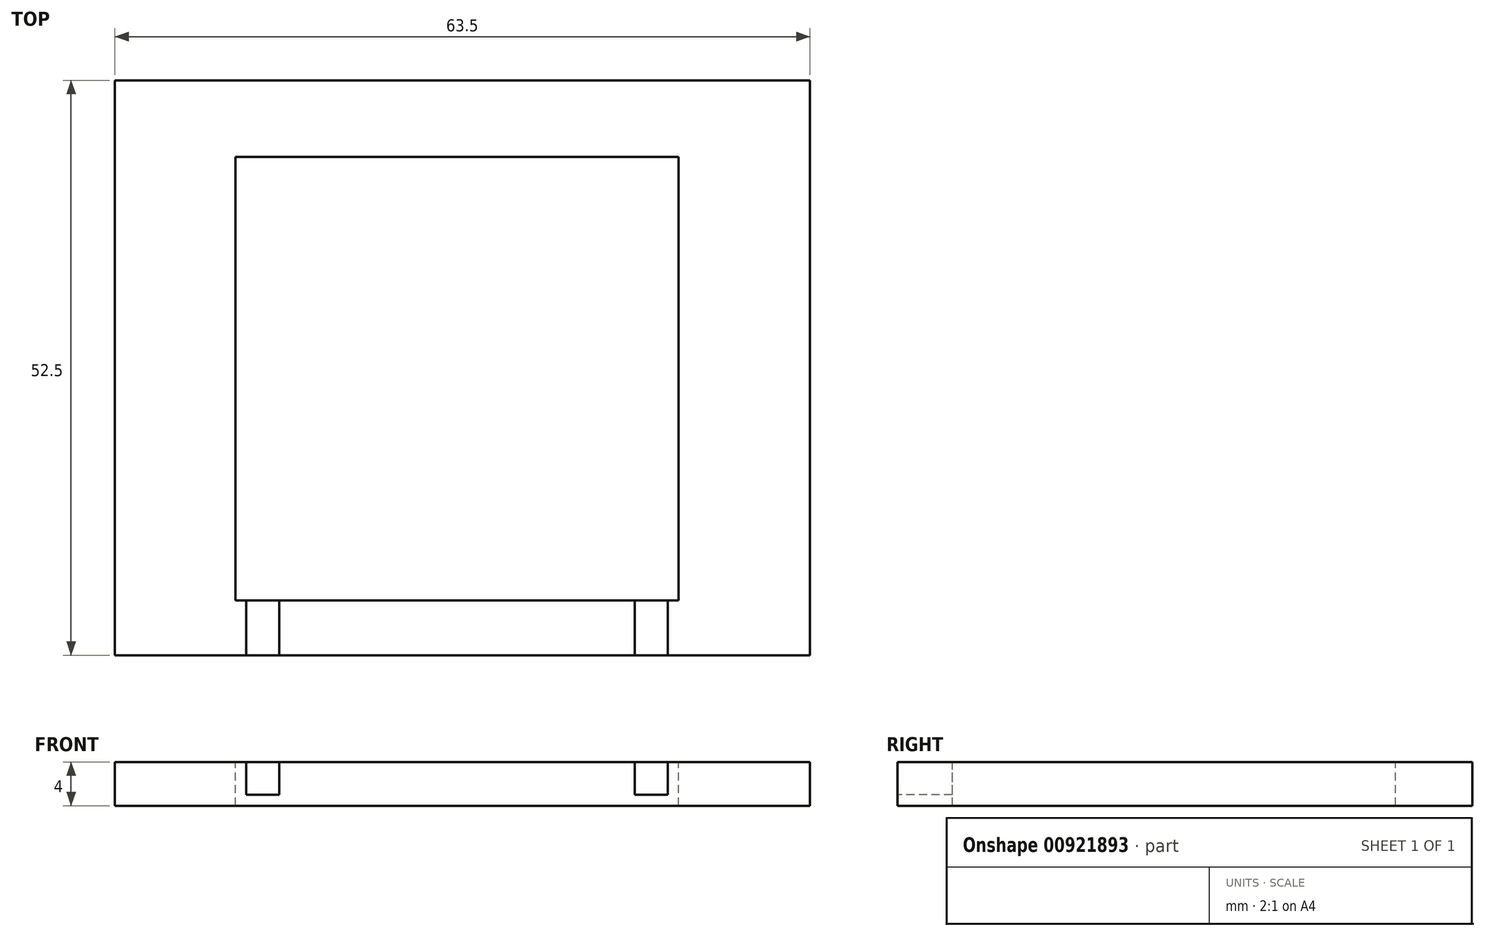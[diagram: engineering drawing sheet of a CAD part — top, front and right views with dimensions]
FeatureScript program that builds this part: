
annotation { "Feature Type Name" : "Feature", "Feature Type Description" : "" }
export const myFeature = defineFeature(function(context is Context, id is Id, definition is map)
    precondition{}
    {
        {
            var Q0;
            Q0=qCreatedBy(makeId("Top.planeOp"),FACE);
            var sketch = newSketch(context, id + "F0", { "sketchPlane" : qUnion([Q0])});
            skLineSegment(sketch, "E0.bottom", {"start": v(0, 0) * mm, "end": v(63.5, 0) * mm});
            skLineSegment(sketch, "E0.top", {"start": v(0, 52.5) * mm, "end": v(63.5, 52.5) * mm});
            skLineSegment(sketch, "E0.left", {"start": v(0, 0) * mm, "end": v(0, 52.5) * mm});
            skLineSegment(sketch, "E0.right", {"start": v(63.5, 0) * mm, "end": v(63.5, 52.5) * mm});
            skSolve(sketch);
        }
        {
            var Q0;
            Q0 = qSketchRegion(id + "F0", true);
            var Q1;
            Q1=makeQuery(id+"F0.imprint","IMPRINT",FACE,{"disambiguationData":[TD([[makeQuery(id+"F0.imprint","IMPRINT",EDGE,{"derivedFrom":sQuery(id+"F0.wireOp",EDGE,"E0.bottom")}),1.0]])]});
            extrude(context, id + "F1", {"entities" : qUnion([Q0, Q1]), "depth" : 4 * mm, "offsetDistance" : 25 * mm});
        }
        {
            var Q0;
            Q0=makeQuery(id+"F1.opExtrude","CAP_FACE",FACE,{"disambiguationData":[OSD([sQuery(id+"F0.wireOp",EDGE,"E0.bottom"),sQuery(id+"F0.wireOp",EDGE,"E0.top"),sQuery(id+"F0.wireOp",EDGE,"E0.left"),sQuery(id+"F0.wireOp",EDGE,"E0.right")])],"isStart":false});
            var sketch = newSketch(context, id + "F2", { "sketchPlane" : qUnion([Q0])});
            skLineSegment(sketch, "E1.bottom", {"start": v(11, 5) * mm, "end": v(51.5, 5) * mm});
            skLineSegment(sketch, "E1.top", {"start": v(11, 45.5) * mm, "end": v(51.5, 45.5) * mm});
            skLineSegment(sketch, "E1.left", {"start": v(11, 5) * mm, "end": v(11, 45.5) * mm});
            skLineSegment(sketch, "E1.right", {"start": v(51.5, 5) * mm, "end": v(51.5, 45.5) * mm});
            skLineSegment(sketch, "E2", {"start": v(12, 5) * mm, "end": v(12, 0) * mm});
            skLineSegment(sketch, "E3", {"start": v(15, 5) * mm, "end": v(15, 0) * mm});
            skLineSegment(sketch, "E4", {"start": v(47.5, 5) * mm, "end": v(47.5, 0) * mm});
            skLineSegment(sketch, "E5", {"start": v(50.5, 5) * mm, "end": v(50.5, 0) * mm});
            skSolve(sketch);
        }
        {
            var Q0;
            {var subQ0=sQuery(id+"F2.wireOp",EDGE,"E2");Q0=makeQuery(id+"F2.imprint","IMPRINT",FACE,{"disambiguationData":[TD([[makeQuery(id+"F2.imprint","IMPRINT",EDGE,{"derivedFrom":subQ0}),1.0]])]});}
            var Q1;
            {var subQ0=sQuery(id+"F2.wireOp",EDGE,"E4");Q1=makeQuery(id+"F2.imprint","IMPRINT",FACE,{"disambiguationData":[TD([[makeQuery(id+"F2.imprint","IMPRINT",EDGE,{"derivedFrom":subQ0}),1.0]])]});}
            extrude(context, id + "F3", {"entities" : qUnion([Q0, Q1]), "operationType" : NewBodyOperationType.REMOVE, "oppositeDirection" : true, "depth" : 3 * mm, "offsetDistance" : 25 * mm});
        }
        {
            var Q0;
            Q0=makeQuery(id+"F2.imprint","IMPRINT",FACE,{"disambiguationData":[TD([[makeQuery(id+"F2.imprint","IMPRINT",EDGE,{"derivedFrom":sQuery(id+"F2.wireOp",EDGE,"E1.top")}),-1.0]])]});
            extrude(context, id + "F4", {"entities" : qUnion([Q0]), "operationType" : NewBodyOperationType.REMOVE, "oppositeDirection" : true, "depth" : 4 * mm, "offsetDistance" : 25 * mm});
        }
    });
